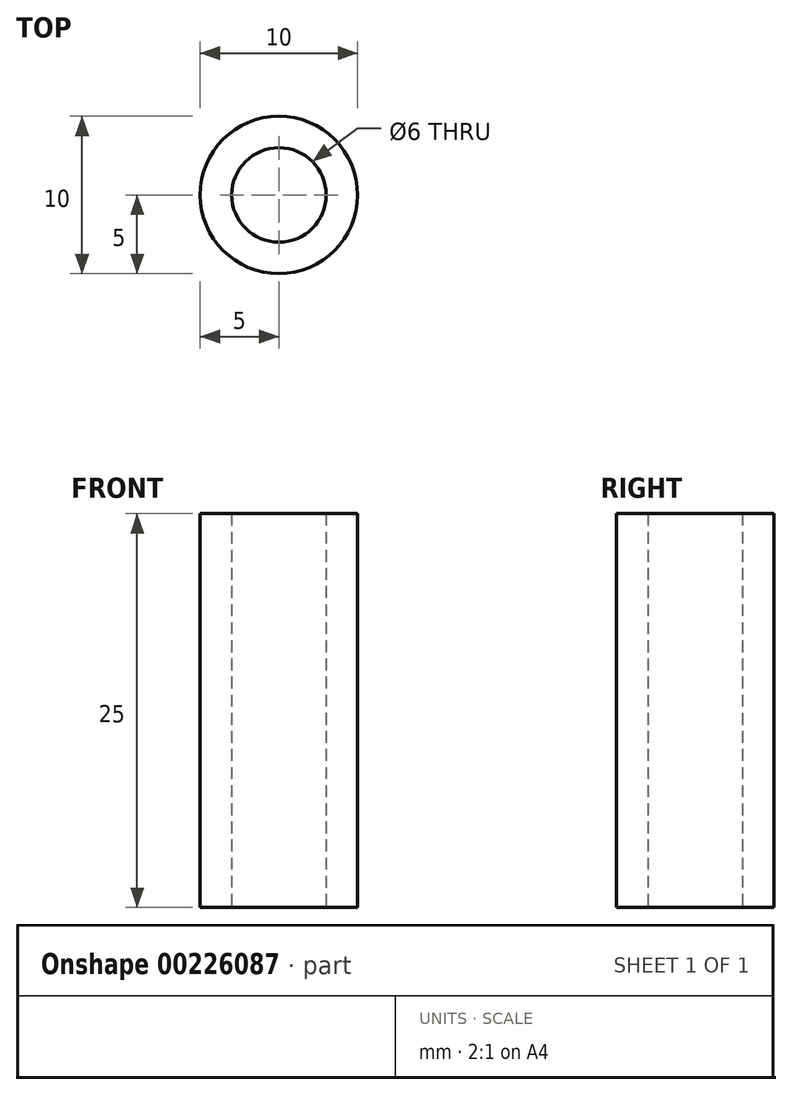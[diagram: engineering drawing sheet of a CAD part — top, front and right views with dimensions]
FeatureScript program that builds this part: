
annotation { "Feature Type Name" : "Feature", "Feature Type Description" : "" }
export const myFeature = defineFeature(function(context is Context, id is Id, definition is map)
    precondition{}
    {
        {
            var Q0;
            Q0=qCreatedBy(makeId("Top.planeOp"),FACE);
            var sketch = newSketch(context, id + "F0", { "sketchPlane" : qUnion([Q0])});
            skCircle(sketch, "E0", {"center": v(0, 0) * mm, "radius": 3 * mm});
            skCircle(sketch, "E1", {"center": v(0, 0) * mm, "radius": 5 * mm});
            skSolve(sketch);
        }
        {
            var Q0;
            Q0 = qSketchRegion(id + "F0", true);
            extrude(context, id + "F1", {"entities" : qUnion([Q0]), "depth" : 25 * mm});
        }
    });
